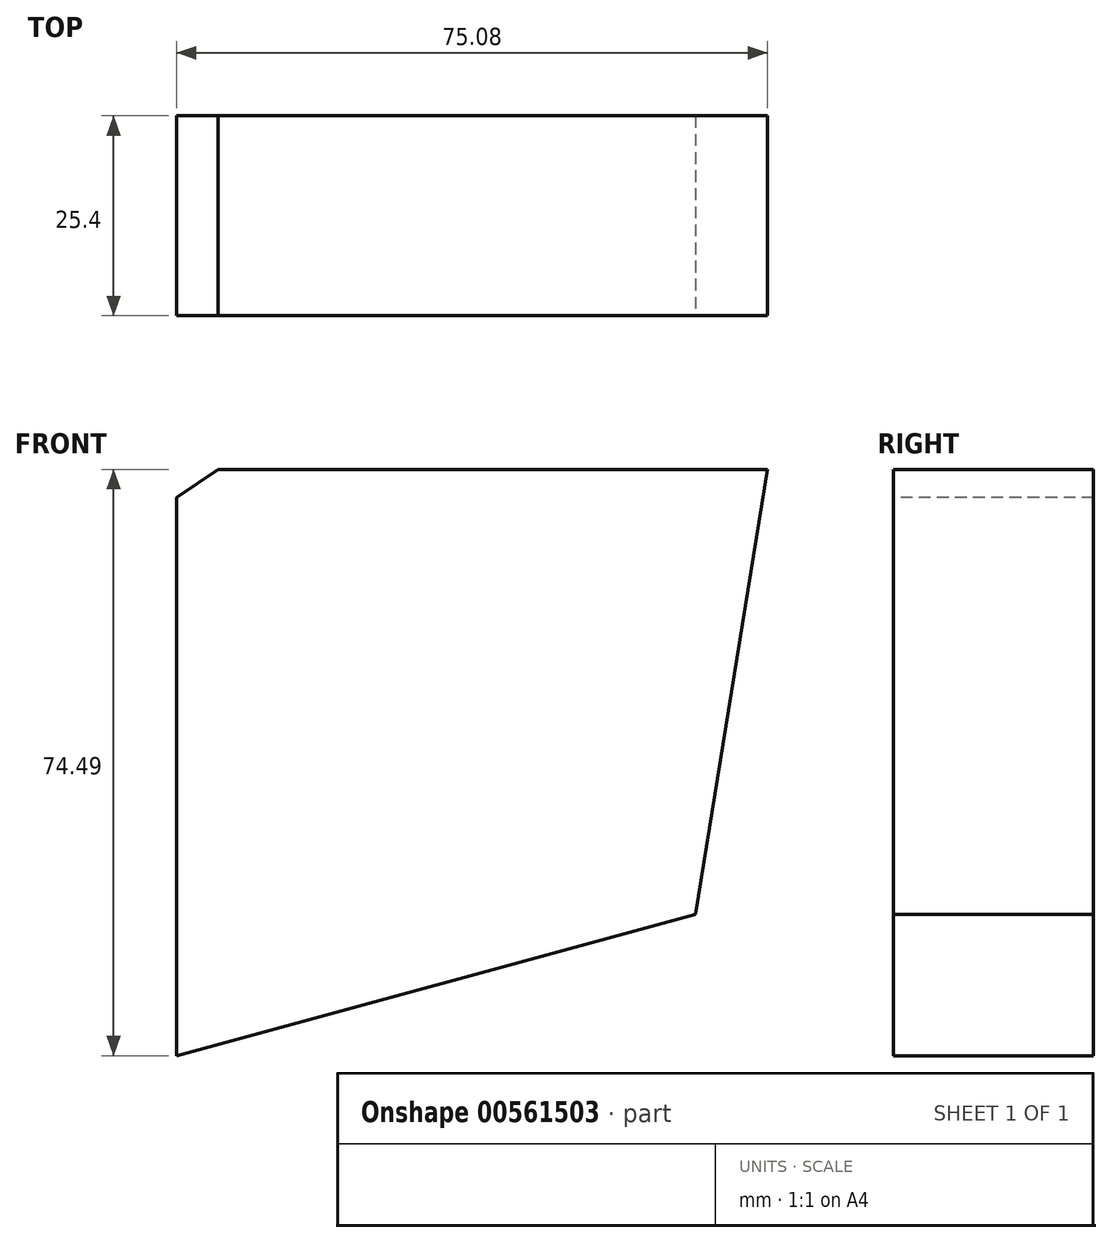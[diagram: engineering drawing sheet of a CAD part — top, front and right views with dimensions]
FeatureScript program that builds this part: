
annotation { "Feature Type Name" : "Feature", "Feature Type Description" : "" }
export const myFeature = defineFeature(function(context is Context, id is Id, definition is map)
    precondition{}
    {
        {
            var Q0;
            Q0=qCreatedBy(makeId("Front.planeOp"),FACE);
            var sketch = newSketch(context, id + "F0", { "sketchPlane" : qUnion([Q0])});
            skLineSegment(sketch, "E0", {"start": v(-53.23, 44.56) * mm, "end": v(16.57, 44.56) * mm});
            skLineSegment(sketch, "E1", {"start": v(16.57, 44.56) * mm, "end": v(7.4, -11.96) * mm});
            skLineSegment(sketch, "E2", {"start": v(7.4, -11.96) * mm, "end": v(-58.51, -29.93) * mm});
            skLineSegment(sketch, "E3", {"start": v(-58.51, -29.93) * mm, "end": v(-58.51, 40.96) * mm});
            skLineSegment(sketch, "E4", {"start": v(-58.51, 40.96) * mm, "end": v(-53.23, 44.56) * mm});
            skSolve(sketch);
        }
        {
            var Q0;
            Q0 = qConstructionFilter(qBodyType(qCreatedBy(id + "F0" ,EDGE), BodyType.WIRE), ConstructionObject.NO);
            extrude(context, id + "F1", {"bodyType" : ToolBodyType.SURFACE, "surfaceEntities" : qUnion([Q0]), "depth" : 25.4 * mm, "offsetDistance" : 25.4 * mm});
        }
    });
